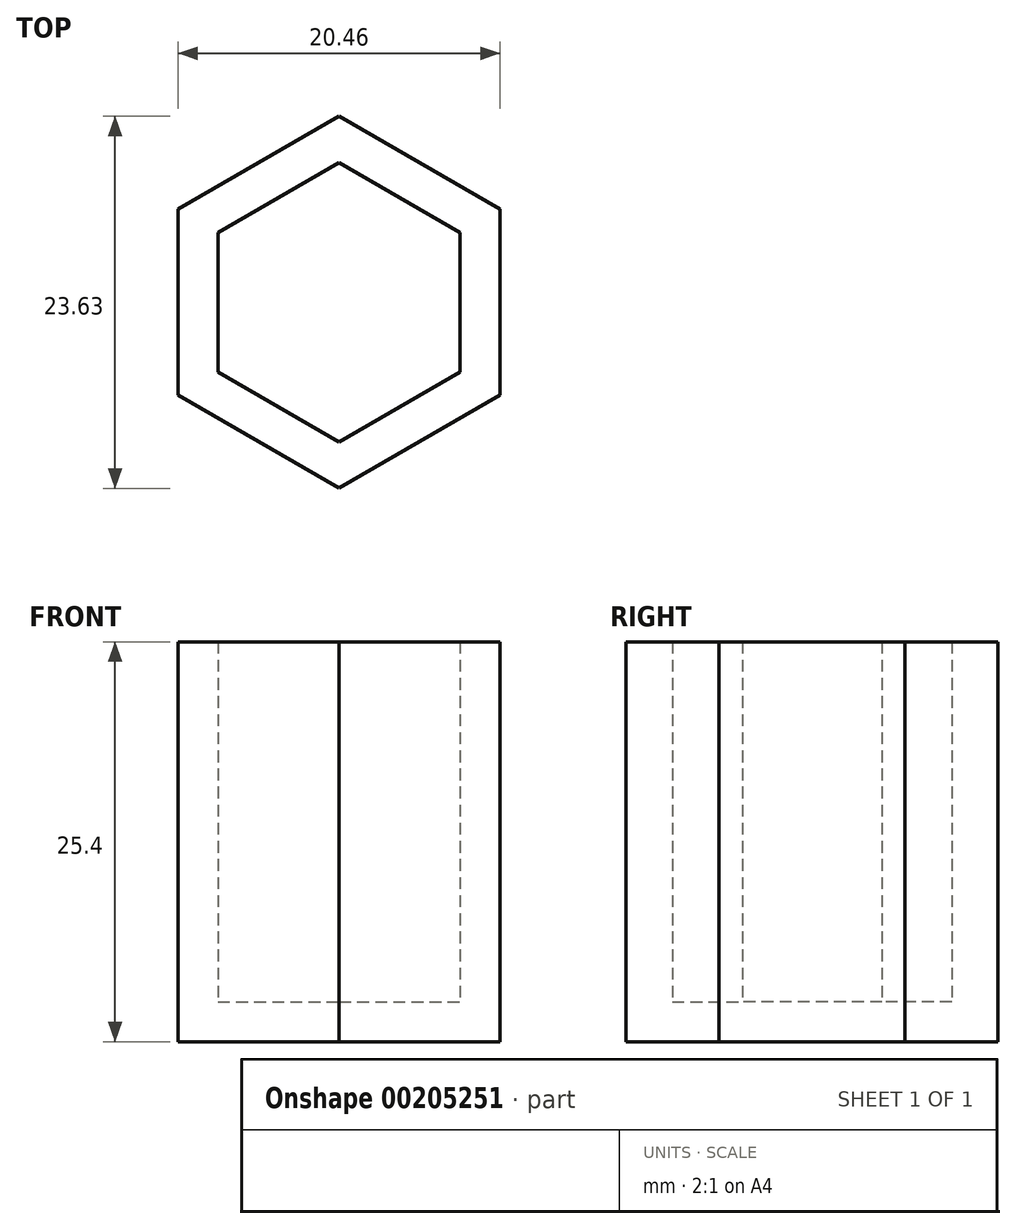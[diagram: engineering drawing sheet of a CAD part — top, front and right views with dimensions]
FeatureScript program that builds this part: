
annotation { "Feature Type Name" : "Feature", "Feature Type Description" : "" }
export const myFeature = defineFeature(function(context is Context, id is Id, definition is map)
    precondition{}
    {
        {
            var Q0;
            Q0=qCreatedBy(makeId("Top.planeOp"),FACE);
            var sketch = newSketch(context, id + "F0", { "sketchPlane" : qUnion([Q0])});
            skCircle(sketch, "E0.cCircle", {"center": v(-44.78, 28.09) * mm, "radius": 10.23 * mm, "construction": true});
            skLineSegment(sketch, "E0.0", {"start": v(-34.55, 34) * mm, "end": v(-34.55, 22.18) * mm});
            skLineSegment(sketch, "E0.1", {"start": v(-34.55, 22.18) * mm, "end": v(-44.78, 16.27) * mm});
            skLineSegment(sketch, "E0.2", {"start": v(-44.78, 16.27) * mm, "end": v(-55.01, 22.18) * mm});
            skLineSegment(sketch, "E0.3", {"start": v(-55.01, 22.18) * mm, "end": v(-55.01, 34) * mm});
            skLineSegment(sketch, "E0.4", {"start": v(-55.01, 34) * mm, "end": v(-44.78, 39.9) * mm});
            skLineSegment(sketch, "E0.5", {"start": v(-44.78, 39.9) * mm, "end": v(-34.55, 34) * mm});
            skPoint(sketch, "E0.0.midPoint", {"position": v(-34.55, 28.09) * mm});
            skSolve(sketch);
        }
        {
            var Q0;
            Q0=makeQuery(id+"F0.imprint","IMPRINT",FACE,{"disambiguationData":[TD([[makeQuery(id+"F0.imprint","IMPRINT",EDGE,{"derivedFrom":sQuery(id+"F0.wireOp",EDGE,"E0.0")}),-1.0]])]});
            extrude(context, id + "F1", {"entities" : qUnion([Q0]), "depth" : 25.4 * mm});
        }
        {
            var Q0;
            Q0=makeQuery(id+"F1.opExtrude","CAP_FACE",FACE,{"disambiguationData":[OSD([sQuery(id+"F0.wireOp",EDGE,"E0.0"),sQuery(id+"F0.wireOp",EDGE,"E0.1"),sQuery(id+"F0.wireOp",EDGE,"E0.2"),sQuery(id+"F0.wireOp",EDGE,"E0.3"),sQuery(id+"F0.wireOp",EDGE,"E0.4"),sQuery(id+"F0.wireOp",EDGE,"E0.5")])],"isStart":false});
            shell(context, id + "F2", {"entities" : qUnion([Q0]), "thickness" : 2.54 * mm});
        }
    });
